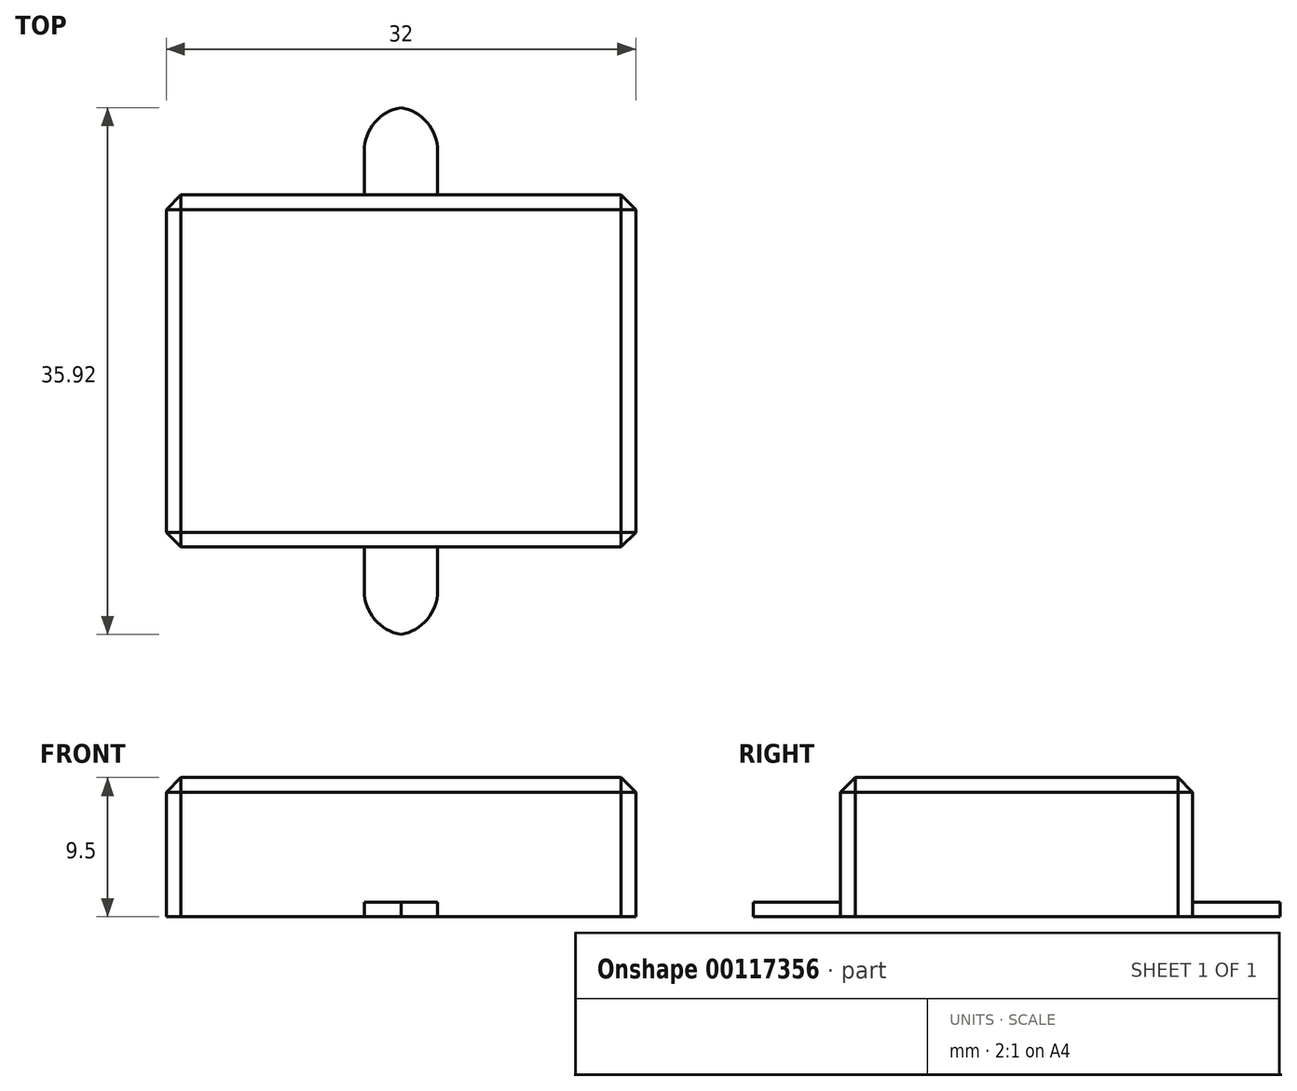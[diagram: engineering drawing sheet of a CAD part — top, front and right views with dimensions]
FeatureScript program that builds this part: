
annotation { "Feature Type Name" : "Feature", "Feature Type Description" : "" }
export const myFeature = defineFeature(function(context is Context, id is Id, definition is map)
    precondition{}
    {
        {
            var Q0;
            Q0=qCreatedBy(makeId("Top.planeOp"),FACE);
            var sketch = newSketch(context, id + "F0", { "sketchPlane" : qUnion([Q0])});
            skLineSegment(sketch, "E0.bottom", {"start": v(16, 12) * mm, "end": v(-16, 12) * mm});
            skLineSegment(sketch, "E0.top", {"start": v(16, -12) * mm, "end": v(-16, -12) * mm});
            skLineSegment(sketch, "E0.left", {"start": v(16, 12) * mm, "end": v(16, -12) * mm});
            skLineSegment(sketch, "E0.right", {"start": v(-16, 12) * mm, "end": v(-16, -12) * mm});
            skPoint(sketch, "E0.middle", {"position": v(0, 0) * mm});
            skLineSegment(sketch, "E1.bottom", {"start": v(2.5, 18) * mm, "end": v(-2.5, 18) * mm});
            skLineSegment(sketch, "E1.top", {"start": v(2.5, 6) * mm, "end": v(-2.5, 6) * mm});
            skLineSegment(sketch, "E1.left", {"start": v(2.5, 18) * mm, "end": v(2.5, 6) * mm});
            skLineSegment(sketch, "E1.right", {"start": v(-2.5, 18) * mm, "end": v(-2.5, 6) * mm});
            skPoint(sketch, "E1.middle", {"position": v(0, 12) * mm});
            skLineSegment(sketch, "E2.MirrorCS", {"start": v(2.5, -18) * mm, "end": v(-2.5, -18) * mm});
            skLineSegment(sketch, "E3.MirrorCS", {"start": v(-2.5, -18) * mm, "end": v(-2.5, -6) * mm});
            skLineSegment(sketch, "E4.MirrorCS", {"start": v(2.5, -18) * mm, "end": v(2.5, -6) * mm});
            skLineSegment(sketch, "E5.MirrorCS", {"start": v(2.5, -6) * mm, "end": v(-2.5, -6) * mm});
            skSolve(sketch);
        }
        {
            var Q0;
            {var subQ9=sQuery(id+"F0.wireOp",EDGE,"E0.left");Q0=makeQuery(id+"F0.imprint","IMPRINT",FACE,{"disambiguationData":[TD([[makeQuery(id+"F0.imprint","IMPRINT",EDGE,{"derivedFrom":subQ9}),-1.0]])]});}
            var Q1;
            {var subQ0=sQuery(id+"F0.wireOp",EDGE,"E5.MirrorCS");Q1=makeQuery(id+"F0.imprint","IMPRINT",FACE,{"disambiguationData":[TD([[makeQuery(id+"F0.imprint","IMPRINT",EDGE,{"derivedFrom":subQ0}),1.0]])]});}
            var Q2;
            {var subQ5=sQuery(id+"F0.wireOp",EDGE,"E1.top");Q2=makeQuery(id+"F0.imprint","IMPRINT",FACE,{"disambiguationData":[TD([[makeQuery(id+"F0.imprint","IMPRINT",EDGE,{"derivedFrom":subQ5}),-1.0]])]});}
            extrude(context, id + "F1", {"entities" : qUnion([Q0, Q1, Q2]), "depth" : 9.5 * mm});
        }
        {
            var Q0;
            {var subQ5=sQuery(id+"F0.wireOp",EDGE,"E1.bottom");Q0=makeQuery(id+"F0.imprint","IMPRINT",FACE,{"disambiguationData":[TD([[makeQuery(id+"F0.imprint","IMPRINT",EDGE,{"derivedFrom":subQ5}),1.0]])]});}
            var Q1;
            {var subQ0=sQuery(id+"F0.wireOp",EDGE,"E2.MirrorCS");Q1=makeQuery(id+"F0.imprint","IMPRINT",FACE,{"disambiguationData":[TD([[makeQuery(id+"F0.imprint","IMPRINT",EDGE,{"derivedFrom":subQ0}),-1.0]])]});}
            extrude(context, id + "F2", {"entities" : qUnion([Q0, Q1]), "operationType" : NewBodyOperationType.ADD, "depth" : 1 * mm});
        }
        {
            var Q0;
            Q0=makeQuery(id+"F2.opExtrude","SWEPT_EDGE",EDGE,{"disambiguationData":[OSD([sQuery(id+"F0.wireOp",EDGE,"E3.MirrorCS"),sQuery(id+"F0.wireOp",EDGE,"E2.MirrorCS")])]});
            var Q1;
            Q1=makeQuery(id+"F2.opExtrude","SWEPT_EDGE",EDGE,{"disambiguationData":[OSD([sQuery(id+"F0.wireOp",EDGE,"E4.MirrorCS"),sQuery(id+"F0.wireOp",EDGE,"E2.MirrorCS")])]});
            var Q2;
            Q2=makeQuery(id+"F2.opExtrude","SWEPT_EDGE",EDGE,{"disambiguationData":[OSD([sQuery(id+"F0.wireOp",EDGE,"E0.top"),sQuery(id+"F0.wireOp",EDGE,"E4.MirrorCS")])]});
            var Q3;
            Q3=makeQuery(id+"F2.opExtrude","SWEPT_EDGE",EDGE,{"disambiguationData":[OSD([sQuery(id+"F0.wireOp",EDGE,"E3.MirrorCS"),sQuery(id+"F0.wireOp",EDGE,"E0.top")])]});
            var Q4;
            Q4=makeQuery(id+"F2.opExtrude","SWEPT_EDGE",EDGE,{"disambiguationData":[OSD([sQuery(id+"F0.wireOp",EDGE,"E0.bottom"),sQuery(id+"F0.wireOp",EDGE,"E1.right")])]});
            var Q5;
            Q5=makeQuery(id+"F2.opExtrude","SWEPT_EDGE",EDGE,{"disambiguationData":[OSD([sQuery(id+"F0.wireOp",EDGE,"E1.bottom"),sQuery(id+"F0.wireOp",EDGE,"E1.right")])]});
            var Q6;
            Q6=makeQuery(id+"F2.opExtrude","SWEPT_EDGE",EDGE,{"disambiguationData":[OSD([sQuery(id+"F0.wireOp",EDGE,"E1.bottom"),sQuery(id+"F0.wireOp",EDGE,"E1.left")])]});
            var Q7;
            Q7=makeQuery(id+"F2.opExtrude","SWEPT_EDGE",EDGE,{"disambiguationData":[OSD([sQuery(id+"F0.wireOp",EDGE,"E0.bottom"),sQuery(id+"F0.wireOp",EDGE,"E1.left")])]});
            fillet(context, id + "F3", {"entities" : qUnion([Q0, Q1, Q2, Q3, Q4, Q5, Q6, Q7]), "radius" : 3 * mm, "tangentPropagation" : true, "allowEdgeOverflow" : false});
        }
        {
            var Q0;
            Q0=makeQuery(id+"F1.opExtrude","CAP_EDGE",EDGE,{"disambiguationData":[OSD([sQuery(id+"F0.wireOp",EDGE,"E0.right")])],"isStart":false});
            var Q1;
            Q1=makeQuery(id+"F1.opExtrude","CAP_EDGE",EDGE,{"disambiguationData":[OSD([sQuery(id+"F0.wireOp",EDGE,"E0.bottom")])],"isStart":false});
            var Q2;
            Q2=makeQuery(id+"F1.opExtrude","CAP_EDGE",EDGE,{"disambiguationData":[OSD([sQuery(id+"F0.wireOp",EDGE,"E0.top")])],"isStart":false});
            var Q3;
            Q3=makeQuery(id+"F1.opExtrude","CAP_EDGE",EDGE,{"disambiguationData":[OSD([sQuery(id+"F0.wireOp",EDGE,"E0.left")])],"isStart":false});
            var Q4;
            Q4=makeQuery(id+"F1.opExtrude","SWEPT_EDGE",EDGE,{"disambiguationData":[OSD([sQuery(id+"F0.wireOp",EDGE,"E0.bottom"),sQuery(id+"F0.wireOp",EDGE,"E0.right")])]});
            var Q5;
            Q5=makeQuery(id+"F1.opExtrude","SWEPT_EDGE",EDGE,{"disambiguationData":[OSD([sQuery(id+"F0.wireOp",EDGE,"E0.right"),sQuery(id+"F0.wireOp",EDGE,"E0.top")])]});
            var Q6;
            Q6=makeQuery(id+"F1.opExtrude","SWEPT_EDGE",EDGE,{"disambiguationData":[OSD([sQuery(id+"F0.wireOp",EDGE,"E0.left"),sQuery(id+"F0.wireOp",EDGE,"E0.top")])]});
            var Q7;
            Q7=makeQuery(id+"F1.opExtrude","SWEPT_EDGE",EDGE,{"disambiguationData":[OSD([sQuery(id+"F0.wireOp",EDGE,"E0.bottom"),sQuery(id+"F0.wireOp",EDGE,"E0.left")])]});
            chamfer(context, id + "F4", {"entities" : qUnion([Q0, Q1, Q2, Q3, Q4, Q5, Q6, Q7]), "width" : 1 * mm, "tangentPropagation" : true});
        }
    });
